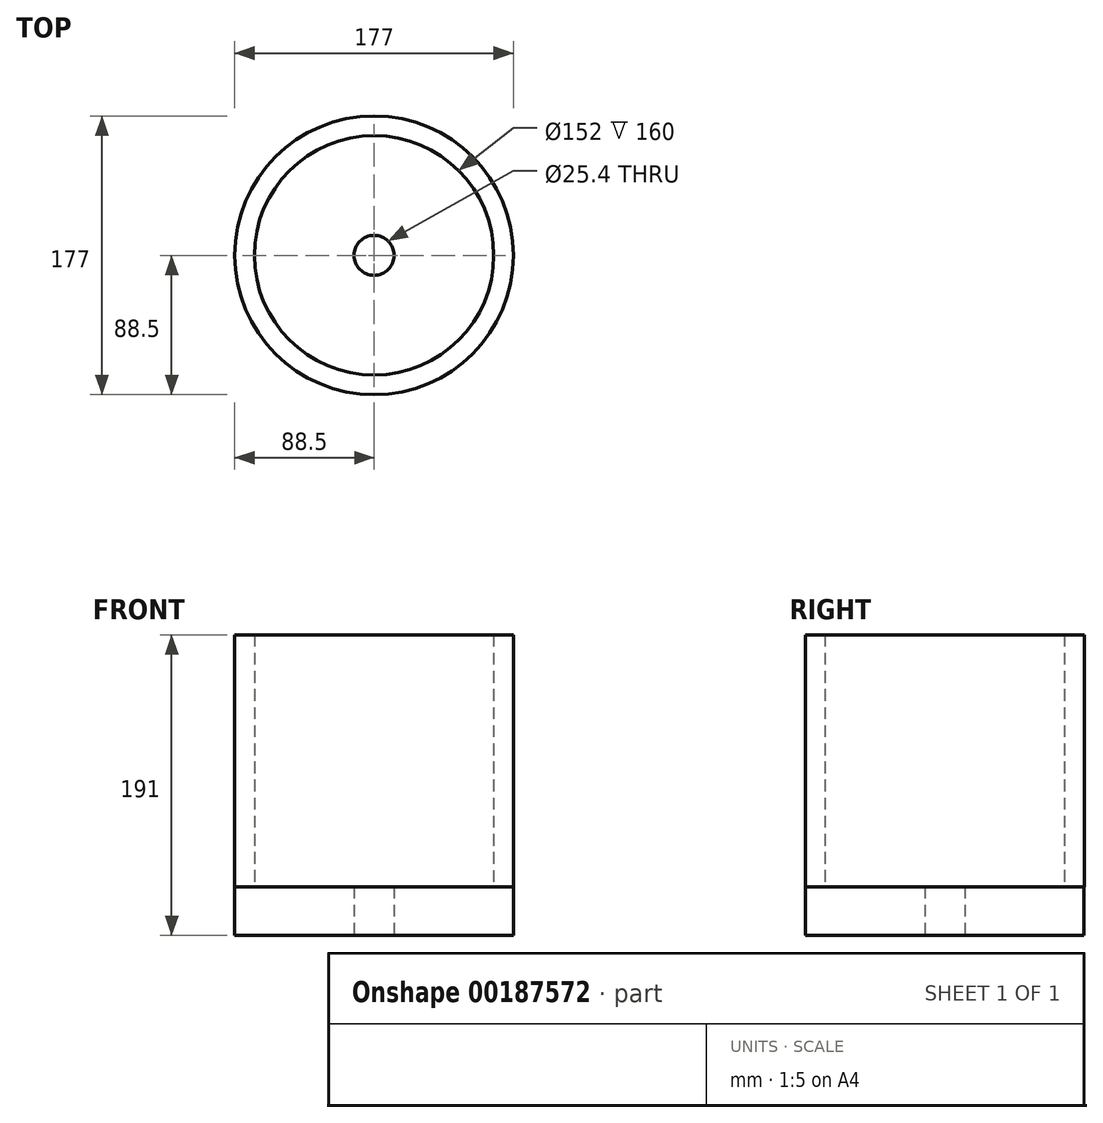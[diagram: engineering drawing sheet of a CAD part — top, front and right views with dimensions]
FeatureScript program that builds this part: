
annotation { "Feature Type Name" : "Feature", "Feature Type Description" : "" }
export const myFeature = defineFeature(function(context is Context, id is Id, definition is map)
    precondition{}
    {
        {
            var Q0;
            Q0=qCreatedBy(makeId("Top.planeOp"),FACE);
            var sketch = newSketch(context, id + "F0", { "sketchPlane" : qUnion([Q0])});
            skCircle(sketch, "E0", {"center": v(0, 0) * mm, "radius": 76 * mm});
            skCircle(sketch, "E1", {"center": v(0, 0) * mm, "radius": 88.5 * mm});
            skSolve(sketch);
        }
        {
            var Q0;
            Q0 = qSketchRegion(id + "F0", true);
            extrude(context, id + "F1", {"entities" : qUnion([Q0]), "depth" : 160 * mm});
        }
        {
            var Q0;
            Q0=makeQuery(id+"F1.opExtrude","CAP_FACE",FACE,{"disambiguationData":[OSD([sQuery(id+"F0.wireOp",EDGE,"E0"),sQuery(id+"F0.wireOp",EDGE,"E1")])],"isStart":true});
            var sketch = newSketch(context, id + "F2", { "sketchPlane" : qUnion([Q0])});
            skCircle(sketch, "E2", {"center": v(0, 0) * mm, "radius": 88.46 * mm});
            skSolve(sketch);
        }
        {
            var Q0;
            Q0 = qSketchRegion(id + "F2", true);
            extrude(context, id + "F3", {"entities" : qUnion([Q0]), "operationType" : NewBodyOperationType.ADD, "depth" : 31 * mm});
        }
        {
            var Q0;
            Q0=makeQuery(id+"F3.opExtrude","CAP_FACE",FACE,{"disambiguationData":[OSD([sQuery(id+"F2.wireOp",EDGE,"E2")])],"isStart":false});
            var sketch = newSketch(context, id + "F4", { "sketchPlane" : qUnion([Q0])});
            skCircle(sketch, "E3", {"center": v(0, 0) * mm, "radius": 12.7 * mm});
            skSolve(sketch);
        }
        {
            var Q0;
            Q0 = qSketchRegion(id + "F4", true);
            extrude(context, id + "F5", {"entities" : qUnion([Q0]), "operationType" : NewBodyOperationType.REMOVE, "endBound" : BoundingType.UP_TO_NEXT, "oppositeDirection" : true, "depth" : 25 * mm});
        }
    });
